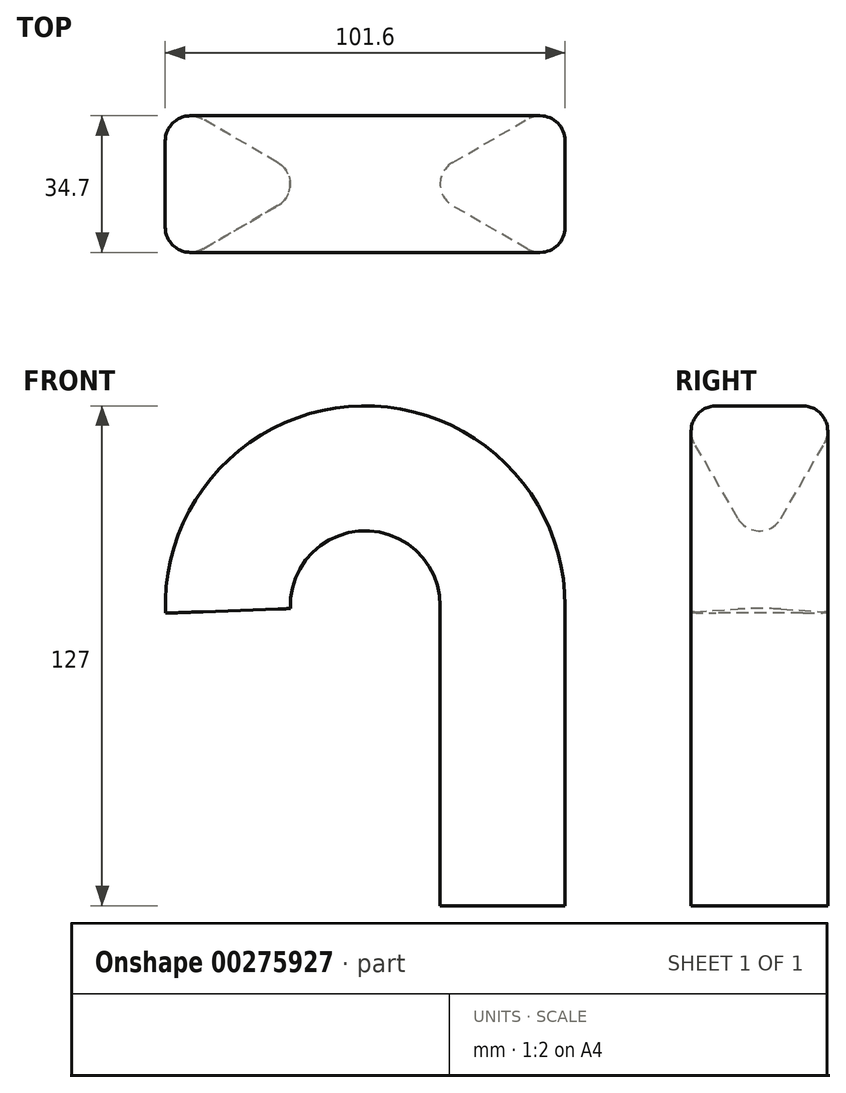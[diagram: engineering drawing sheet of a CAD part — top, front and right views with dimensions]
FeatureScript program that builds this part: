
annotation { "Feature Type Name" : "Feature", "Feature Type Description" : "" }
export const myFeature = defineFeature(function(context is Context, id is Id, definition is map)
    precondition{}
    {
        {
            var Q0;
            Q0=qCreatedBy(makeId("Front.planeOp"),FACE);
            var sketch = newSketch(context, id + "F0", { "sketchPlane" : qUnion([Q0])});
            skLineSegment(sketch, "E0", {"start": v(0, 0) * mm, "end": v(0, 76.2) * mm});
            skArc(sketch, "E1", {"start": v(0, 76.2) * mm, "mid": v(-38.8, 114.3) * mm, "end": v(-76.17, 74.8) * mm});
            skSolve(sketch);
        }
        {
            var Q0;
            Q0=qCreatedBy(makeId("Top.planeOp"),FACE);
            var sketch = newSketch(context, id + "F1", { "sketchPlane" : qUnion([Q0])});
            skCircle(sketch, "E2.cCircle", {"center": v(0, 0) * mm, "radius": 12.7 * mm, "construction": true});
            skLineSegment(sketch, "E2.0", {"start": v(12.7, 11) * mm, "end": v(12.7, -11) * mm});
            skLineSegment(sketch, "E2.1", {"start": v(3.18, -16.5) * mm, "end": v(-15.88, -5.5) * mm});
            skLineSegment(sketch, "E2.2", {"start": v(-15.88, 5.5) * mm, "end": v(3.18, 16.5) * mm});
            skPoint(sketch, "E2.0.midPoint", {"position": v(12.7, 0) * mm});
            skPoint(sketch, "E3.visualSharp", {"position": v(-25.4, 0) * mm});
            skArc(sketch, "E3.filletArc", {"start": v(-15.88, 5.5) * mm, "mid": v(-19.05, 0) * mm, "end": v(-15.88, -5.5) * mm});
            skPoint(sketch, "E4.visualSharp", {"position": v(12.7, -22) * mm});
            skArc(sketch, "E4.filletArc", {"start": v(3.18, -16.5) * mm, "mid": v(9.53, -16.5) * mm, "end": v(12.7, -11) * mm});
            skPoint(sketch, "E5.visualSharp", {"position": v(12.7, 22) * mm});
            skArc(sketch, "E5.filletArc", {"start": v(12.7, 11) * mm, "mid": v(9.53, 16.5) * mm, "end": v(3.18, 16.5) * mm});
            skSolve(sketch);
        }
        {
            var Q0;
            Q0=makeQuery(id+"F1.imprint","IMPRINT",FACE,{"disambiguationData":[TD([[makeQuery(id+"F1.imprint","IMPRINT",EDGE,{"derivedFrom":sQuery(id+"F1.wireOp",EDGE,"E2.0")}),-1.0]])]});
            var Q1;
            Q1=sQuery(id+"F0.wireOp",EDGE,"E1");
            var Q2;
            Q2=sQuery(id+"F0.wireOp",EDGE,"E0");
            sweep(context, id + "F2", {"profiles" : qUnion([Q0]), "path" : qUnion([Q1, Q2])});
        }
    });
